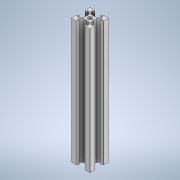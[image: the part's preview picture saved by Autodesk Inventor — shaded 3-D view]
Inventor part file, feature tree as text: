
AUTODESK INVENTOR PART (.ipt)
format: ipt  version: 2021 (Build 250183000, 183)  size: 234,496 bytes
history: native  units: mm
features: sketch x3, extrude x2, fillet x2, other x1, pattern_circular x1, hole x1, projected_geometry x1
ambient origin geometry x8: Origin, YZ Plane, XZ Plane, XY Plane, X Axis, Y Axis, Z Axis, Center Point
bodies: Body1 (feature_tree)
feature tree (11):
  other  "實體1"
  extrude  "擠出1"  Depth=20.0mm
  extrude  "擠出2"  Depth=20.0mm
  fillet  "圓角1"  Radius=134.0mm
  pattern_circular  "環形陣列1"  [2 undecoded]
  hole  "孔1"  [1 undecoded]
  fillet  "圓角2"  Radius=6.2mm
  sketch  "草圖1"
  sketch  "草圖2"
  projected_geometry  "投影迴路1"
  sketch  "草圖3"
note: 3 required parameter values undecoded (feature->parameter linkage not recoverable at this tier; creation-order binding heuristic only, values carry confidence <= 0.55)
